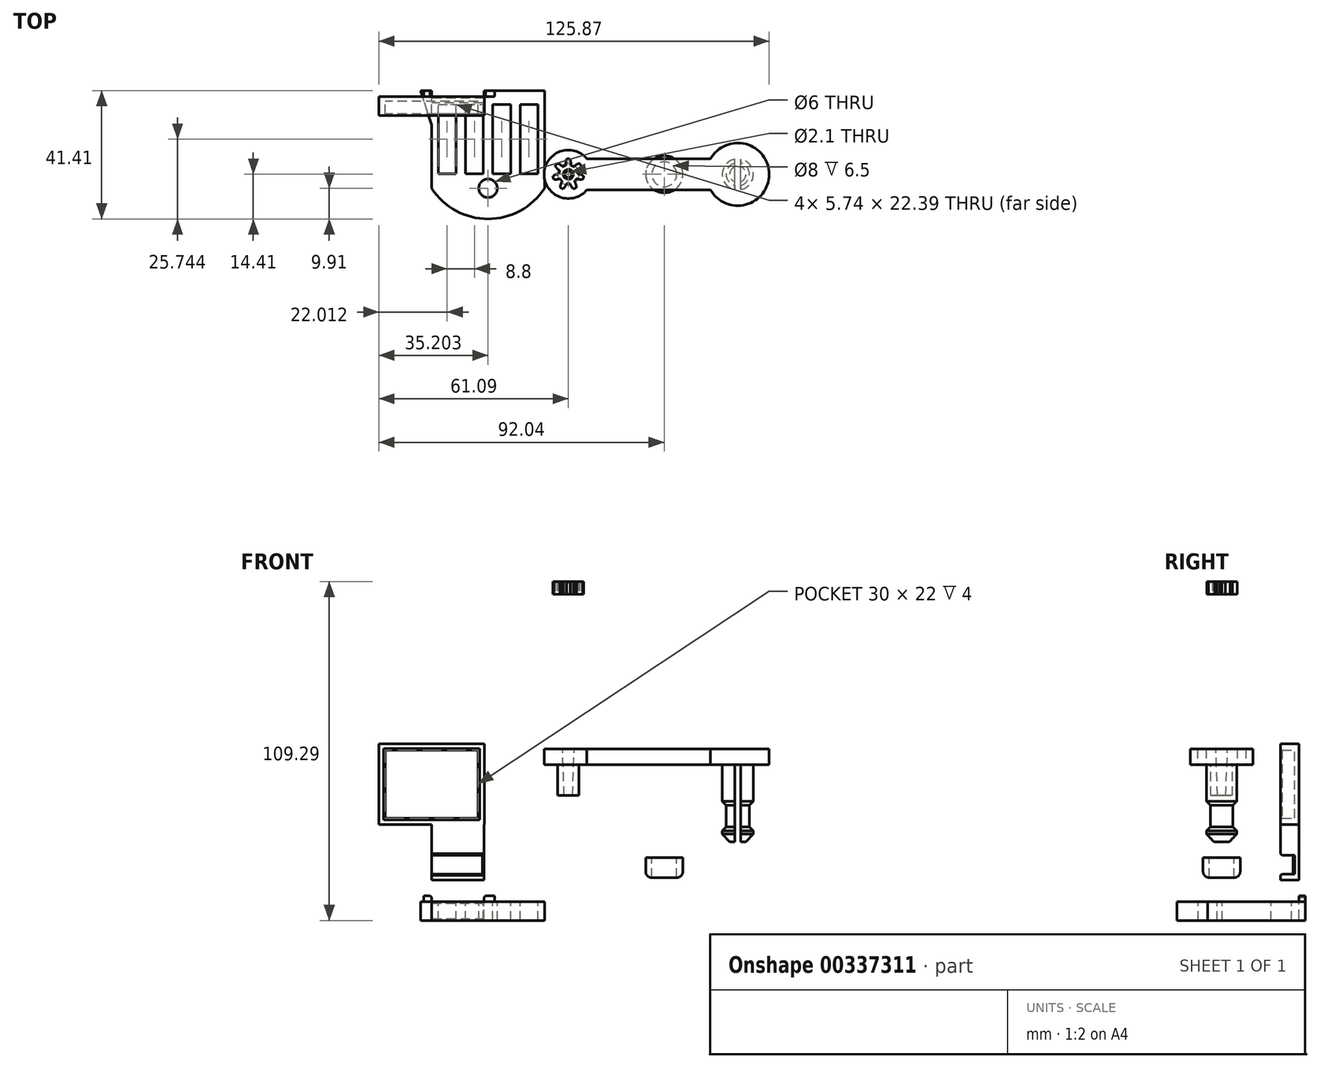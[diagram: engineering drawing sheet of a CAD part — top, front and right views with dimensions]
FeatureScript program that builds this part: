
annotation { "Feature Type Name" : "Feature", "Feature Type Description" : "" }
export const myFeature = defineFeature(function(context is Context, id is Id, definition is map)
    precondition{}
    {
        {
            var Q0;
            Q0=qCreatedBy(makeId("Top.planeOp"),FACE);
            cPlane(context, id + "F0", {"entities" : qUnion([Q0]), "cplaneType" : CPlaneType.OFFSET, "offset" : 25 * mm, "width" : 150 * mm, "height" : 150 * mm});
        }
        {
            var Q0;
            Q0=qCreatedBy(id+"F0.planeOp",FACE);
            var sketch = newSketch(context, id + "F1", { "sketchPlane" : qUnion([Q0])});
            skCircle(sketch, "E0", {"center": v(0, 0) * mm, "radius": 3 * mm, "construction": true});
            skCircle(sketch, "E1", {"center": v(0, 0) * mm, "radius": 5 * mm, "construction": true});
            skArc(sketch, "E2", {"start": v(0.5, 4.97) * mm, "mid": v(0, 5) * mm, "end": v(-0.5, 4.97) * mm});
            skArc(sketch, "E3", {"start": v(-0.5, 4.97) * mm, "mid": v(-0.8, 3.96) * mm, "end": v(-0.77, 2.9) * mm});
            skArc(sketch, "E4.MirrorCS", {"start": v(0.5, 4.97) * mm, "mid": v(0.8, 3.96) * mm, "end": v(0.77, 2.9) * mm});
            skArc(sketch, "E5.1.0", {"start": v(-4.2, 2.71) * mm, "mid": v(-3.6, 1.84) * mm, "end": v(-2.75, 1.2) * mm});
            skArc(sketch, "E5.1.1", {"start": v(-3.58, 3.5) * mm, "mid": v(-3.9, 3.12) * mm, "end": v(-4.2, 2.71) * mm});
            skArc(sketch, "E5.1.2", {"start": v(-3.58, 3.5) * mm, "mid": v(-2.6, 3.1) * mm, "end": v(-1.78, 2.41) * mm});
            skArc(sketch, "E5.2.0", {"start": v(-4.74, -1.6) * mm, "mid": v(-3.68, -1.67) * mm, "end": v(-2.65, -1.4) * mm});
            skArc(sketch, "E5.2.1", {"start": v(-4.96, -0.62) * mm, "mid": v(-4.87, -1.11) * mm, "end": v(-4.74, -1.6) * mm});
            skArc(sketch, "E5.2.2", {"start": v(-4.96, -0.62) * mm, "mid": v(-4.04, -0.1) * mm, "end": v(-3, 0.1) * mm});
            skArc(sketch, "E5.3.0", {"start": v(-1.7, -4.7) * mm, "mid": v(-0.99, -3.92) * mm, "end": v(-0.56, -2.95) * mm});
            skArc(sketch, "E5.3.1", {"start": v(-2.6, -4.27) * mm, "mid": v(-2.17, -4.5) * mm, "end": v(-1.7, -4.7) * mm});
            skArc(sketch, "E5.3.2", {"start": v(-2.6, -4.27) * mm, "mid": v(-2.45, -3.22) * mm, "end": v(-1.95, -2.28) * mm});
            skArc(sketch, "E5.4.0", {"start": v(2.6, -4.27) * mm, "mid": v(2.45, -3.22) * mm, "end": v(1.95, -2.28) * mm});
            skArc(sketch, "E5.4.1", {"start": v(1.7, -4.7) * mm, "mid": v(2.17, -4.5) * mm, "end": v(2.6, -4.27) * mm});
            skArc(sketch, "E5.4.2", {"start": v(1.7, -4.7) * mm, "mid": v(0.99, -3.92) * mm, "end": v(0.56, -2.95) * mm});
            skArc(sketch, "E5.5.0", {"start": v(4.96, -0.62) * mm, "mid": v(4.04, -0.1) * mm, "end": v(3, 0.1) * mm});
            skArc(sketch, "E5.5.1", {"start": v(4.74, -1.6) * mm, "mid": v(4.87, -1.11) * mm, "end": v(4.96, -0.62) * mm});
            skArc(sketch, "E5.5.2", {"start": v(4.74, -1.6) * mm, "mid": v(3.68, -1.67) * mm, "end": v(2.65, -1.4) * mm});
            skArc(sketch, "E5.6.0", {"start": v(3.58, 3.5) * mm, "mid": v(2.6, 3.1) * mm, "end": v(1.78, 2.41) * mm});
            skArc(sketch, "E5.6.1", {"start": v(4.2, 2.71) * mm, "mid": v(3.9, 3.12) * mm, "end": v(3.58, 3.5) * mm});
            skArc(sketch, "E5.6.2", {"start": v(4.2, 2.71) * mm, "mid": v(3.6, 1.84) * mm, "end": v(2.75, 1.2) * mm});
            skArc(sketch, "E6", {"start": v(1.78, 2.41) * mm, "mid": v(1.3, 2.7) * mm, "end": v(0.77, 2.9) * mm});
            skArc(sketch, "E7.1.0", {"start": v(-0.77, 2.9) * mm, "mid": v(-1.3, 2.7) * mm, "end": v(-1.78, 2.41) * mm});
            skArc(sketch, "E7.2.0", {"start": v(-2.75, 1.2) * mm, "mid": v(-2.93, 0.67) * mm, "end": v(-3, 0.1) * mm});
            skArc(sketch, "E7.3.0", {"start": v(-2.65, -1.4) * mm, "mid": v(-2.35, -1.87) * mm, "end": v(-1.95, -2.28) * mm});
            skArc(sketch, "E7.4.0", {"start": v(-0.56, -2.95) * mm, "mid": v(0, -3) * mm, "end": v(0.56, -2.95) * mm});
            skArc(sketch, "E7.5.0", {"start": v(1.95, -2.28) * mm, "mid": v(2.35, -1.87) * mm, "end": v(2.65, -1.4) * mm});
            skArc(sketch, "E7.6.0", {"start": v(3, 0.1) * mm, "mid": v(2.93, 0.67) * mm, "end": v(2.75, 1.2) * mm});
            skSolve(sketch);
        }
        {
            var Q0;
            Q0 = qSketchRegion(id + "F1", true);
            extrude(context, id + "F2", {"entities" : qUnion([Q0]), "depth" : 4 * mm});
        }
        {
            var Q0;
            Q0=qCreatedBy(id+"F0.planeOp",FACE);
            var sketch = newSketch(context, id + "F3", { "sketchPlane" : qUnion([Q0])});
            skCircle(sketch, "E8", {"center": v(0, 0) * mm, "radius": 1.05 * mm});
            skSolve(sketch);
        }
        {
            var Q0;
            Q0 = qSketchRegion(id + "F3", true);
            extrude(context, id + "F4", {"entities" : qUnion([Q0]), "operationType" : NewBodyOperationType.REMOVE, "depth" : 25 * mm});
        }
        {
            var Q0;
            Q0=makeQuery(id+"F4.boolean.opBoolean","COPY",EDGE,{"derivedFrom":makeQuery(id+"F4.opExtrude","CAP_EDGE",EDGE,{"disambiguationData":[OSD([sQuery(id+"F3.wireOp",EDGE,"E8")])],"isStart":true})});
            var Q1;
            Q1=makeQuery(id+"F4.boolean.opBoolean","INTERSECT",EDGE,{"derivedFrom":[makeQuery(id+"F2.opExtrude","CAP_FACE",FACE,{"disambiguationData":[OSD([sQuery(id+"F1.wireOp",EDGE,"E2"),sQuery(id+"F1.wireOp",EDGE,"E3"),sQuery(id+"F1.wireOp",EDGE,"E4.MirrorCS"),sQuery(id+"F1.wireOp",EDGE,"E5.1.0"),sQuery(id+"F1.wireOp",EDGE,"E5.1.1"),sQuery(id+"F1.wireOp",EDGE,"E5.1.2"),sQuery(id+"F1.wireOp",EDGE,"E5.2.0"),sQuery(id+"F1.wireOp",EDGE,"E5.2.1"),sQuery(id+"F1.wireOp",EDGE,"E5.2.2"),sQuery(id+"F1.wireOp",EDGE,"E5.3.0"),sQuery(id+"F1.wireOp",EDGE,"E5.3.1"),sQuery(id+"F1.wireOp",EDGE,"E5.3.2"),sQuery(id+"F1.wireOp",EDGE,"E5.4.0"),sQuery(id+"F1.wireOp",EDGE,"E5.4.1"),sQuery(id+"F1.wireOp",EDGE,"E5.4.2"),sQuery(id+"F1.wireOp",EDGE,"E5.5.0"),sQuery(id+"F1.wireOp",EDGE,"E5.5.1"),sQuery(id+"F1.wireOp",EDGE,"E5.5.2"),sQuery(id+"F1.wireOp",EDGE,"E5.6.0"),sQuery(id+"F1.wireOp",EDGE,"E5.6.1"),sQuery(id+"F1.wireOp",EDGE,"E5.6.2"),sQuery(id+"F1.wireOp",EDGE,"E6"),sQuery(id+"F1.wireOp",EDGE,"E7.1.0"),sQuery(id+"F1.wireOp",EDGE,"E7.2.0"),sQuery(id+"F1.wireOp",EDGE,"E7.3.0"),sQuery(id+"F1.wireOp",EDGE,"E7.4.0"),sQuery(id+"F1.wireOp",EDGE,"E7.5.0"),sQuery(id+"F1.wireOp",EDGE,"E7.6.0")])],"isStart":false}),makeQuery(id+"F4.opExtrude","SWEPT_FACE",FACE,{"disambiguationData":[OSD([sQuery(id+"F3.wireOp",EDGE,"E8")])]})]});
            chamfer(context, id + "F5", {"entities" : qUnion([Q0, Q1]), "width" : .5 * mm, "tangentPropagation" : true});
        }
        {
            var Q0;
            Q0=qCreatedBy(makeId("Top.planeOp"),FACE);
            var sketch = newSketch(context, id + "F6", { "sketchPlane" : qUnion([Q0])});
            skCircle(sketch, "E9", {"center": v(0, 0) * mm, "radius": 15 * mm, "construction": true});
            skCircle(sketch, "E10", {"center": v(0, 0) * mm, "radius": 17 * mm, "construction": true});
            skLineSegment(sketch, "E11", {"start": v(0, 19.59) * mm, "end": v(0, -20.8) * mm, "construction": true});
            skArc(sketch, "E12", {"start": v(0.5, 17) * mm, "mid": v(0, 17) * mm, "end": v(-0.5, 17) * mm});
            skArc(sketch, "E13", {"start": v(-0.5, 17) * mm, "mid": v(-0.8, 16) * mm, "end": v(-0.77, 14.98) * mm});
            skArc(sketch, "E14.MirrorCS", {"start": v(0.5, 17) * mm, "mid": v(0.8, 16) * mm, "end": v(0.77, 14.98) * mm});
            skArc(sketch, "E15.1.0", {"start": v(-4.02, 16.52) * mm, "mid": v(-4.1, 15.5) * mm, "end": v(-3.87, 14.5) * mm});
            skArc(sketch, "E15.1.1", {"start": v(-3.04, 16.73) * mm, "mid": v(-3.53, 16.63) * mm, "end": v(-4.02, 16.52) * mm});
            skArc(sketch, "E15.1.2", {"start": v(-3.04, 16.73) * mm, "mid": v(-2.55, 15.82) * mm, "end": v(-2.36, 14.81) * mm});
            skArc(sketch, "E15.2.0", {"start": v(-7.37, 15.32) * mm, "mid": v(-7.24, 14.3) * mm, "end": v(-6.8, 13.37) * mm});
            skArc(sketch, "E15.2.1", {"start": v(-6.45, 15.73) * mm, "mid": v(-6.91, 15.53) * mm, "end": v(-7.37, 15.32) * mm});
            skArc(sketch, "E15.2.2", {"start": v(-6.45, 15.73) * mm, "mid": v(-5.78, 14.95) * mm, "end": v(-5.39, 14) * mm});
            skArc(sketch, "E15.3.0", {"start": v(-10.4, 13.45) * mm, "mid": v(-10.05, 12.48) * mm, "end": v(-9.43, 11.67) * mm});
            skArc(sketch, "E15.3.1", {"start": v(-9.58, 14.04) * mm, "mid": v(-10, 13.75) * mm, "end": v(-10.4, 13.45) * mm});
            skArc(sketch, "E15.3.2", {"start": v(-9.58, 14.04) * mm, "mid": v(-8.77, 13.42) * mm, "end": v(-8.18, 12.57) * mm});
            skArc(sketch, "E15.4.0", {"start": v(-12.96, 11) * mm, "mid": v(-12.43, 10.12) * mm, "end": v(-11.65, 9.45) * mm});
            skArc(sketch, "E15.4.1", {"start": v(-12.3, 11.74) * mm, "mid": v(-12.63, 11.38) * mm, "end": v(-12.96, 11) * mm});
            skArc(sketch, "E15.4.2", {"start": v(-12.3, 11.74) * mm, "mid": v(-11.36, 11.3) * mm, "end": v(-10.62, 10.6) * mm});
            skArc(sketch, "E15.5.0", {"start": v(-14.97, 8.06) * mm, "mid": v(-14.26, 7.31) * mm, "end": v(-13.36, 6.82) * mm});
            skArc(sketch, "E15.5.1", {"start": v(-14.47, 8.93) * mm, "mid": v(-14.72, 8.5) * mm, "end": v(-14.97, 8.06) * mm});
            skArc(sketch, "E15.5.2", {"start": v(-14.47, 8.93) * mm, "mid": v(-13.47, 8.7) * mm, "end": v(-12.59, 8.16) * mm});
            skArc(sketch, "E15.6.0", {"start": v(-16.32, 4.78) * mm, "mid": v(-15.47, 4.19) * mm, "end": v(-14.48, 3.9) * mm});
            skArc(sketch, "E15.6.1", {"start": v(-16, 5.73) * mm, "mid": v(-16.17, 5.25) * mm, "end": v(-16.32, 4.78) * mm});
            skArc(sketch, "E15.6.2", {"start": v(-16, 5.73) * mm, "mid": v(-14.98, 5.7) * mm, "end": v(-14, 5.36) * mm});
            skArc(sketch, "E15.7.0", {"start": v(-16.95, 1.28) * mm, "mid": v(-16, 0.88) * mm, "end": v(-14.98, 0.8) * mm});
            skArc(sketch, "E15.7.1", {"start": v(-16.85, 2.27) * mm, "mid": v(-16.9, 1.78) * mm, "end": v(-16.95, 1.28) * mm});
            skArc(sketch, "E15.7.2", {"start": v(-16.85, 2.27) * mm, "mid": v(-15.84, 2.47) * mm, "end": v(-14.82, 2.33) * mm});
            skArc(sketch, "E15.8.0", {"start": v(-16.85, -2.27) * mm, "mid": v(-15.84, -2.47) * mm, "end": v(-14.82, -2.33) * mm});
            skArc(sketch, "E15.8.1", {"start": v(-16.95, -1.28) * mm, "mid": v(-16.9, -1.78) * mm, "end": v(-16.85, -2.27) * mm});
            skArc(sketch, "E15.8.2", {"start": v(-16.95, -1.28) * mm, "mid": v(-16, -0.88) * mm, "end": v(-14.98, -0.8) * mm});
            skArc(sketch, "E15.9.0", {"start": v(-16, -5.73) * mm, "mid": v(-14.98, -5.7) * mm, "end": v(-14, -5.36) * mm});
            skArc(sketch, "E15.9.1", {"start": v(-16.32, -4.78) * mm, "mid": v(-16.17, -5.25) * mm, "end": v(-16, -5.73) * mm});
            skArc(sketch, "E15.9.2", {"start": v(-16.32, -4.78) * mm, "mid": v(-15.47, -4.19) * mm, "end": v(-14.48, -3.9) * mm});
            skArc(sketch, "E15.10.0", {"start": v(-14.47, -8.93) * mm, "mid": v(-13.47, -8.7) * mm, "end": v(-12.59, -8.16) * mm});
            skArc(sketch, "E15.10.1", {"start": v(-14.97, -8.06) * mm, "mid": v(-14.72, -8.5) * mm, "end": v(-14.47, -8.93) * mm});
            skArc(sketch, "E15.10.2", {"start": v(-14.97, -8.06) * mm, "mid": v(-14.26, -7.31) * mm, "end": v(-13.36, -6.82) * mm});
            skArc(sketch, "E15.11.0", {"start": v(-12.3, -11.74) * mm, "mid": v(-11.36, -11.3) * mm, "end": v(-10.62, -10.6) * mm});
            skArc(sketch, "E15.11.1", {"start": v(-12.96, -11) * mm, "mid": v(-12.63, -11.38) * mm, "end": v(-12.3, -11.74) * mm});
            skArc(sketch, "E15.11.2", {"start": v(-12.96, -11) * mm, "mid": v(-12.43, -10.12) * mm, "end": v(-11.65, -9.45) * mm});
            skArc(sketch, "E15.12.0", {"start": v(-9.58, -14.04) * mm, "mid": v(-8.77, -13.42) * mm, "end": v(-8.18, -12.57) * mm});
            skArc(sketch, "E15.12.1", {"start": v(-10.4, -13.45) * mm, "mid": v(-10, -13.75) * mm, "end": v(-9.58, -14.04) * mm});
            skArc(sketch, "E15.12.2", {"start": v(-10.4, -13.45) * mm, "mid": v(-10.05, -12.48) * mm, "end": v(-9.43, -11.67) * mm});
            skArc(sketch, "E15.13.0", {"start": v(-6.45, -15.73) * mm, "mid": v(-5.78, -14.95) * mm, "end": v(-5.39, -14) * mm});
            skArc(sketch, "E15.13.1", {"start": v(-7.37, -15.32) * mm, "mid": v(-6.91, -15.53) * mm, "end": v(-6.45, -15.73) * mm});
            skArc(sketch, "E15.13.2", {"start": v(-7.37, -15.32) * mm, "mid": v(-7.24, -14.3) * mm, "end": v(-6.8, -13.37) * mm});
            skArc(sketch, "E15.14.0", {"start": v(-3.04, -16.73) * mm, "mid": v(-2.55, -15.82) * mm, "end": v(-2.36, -14.81) * mm});
            skArc(sketch, "E15.14.1", {"start": v(-4.02, -16.52) * mm, "mid": v(-3.53, -16.63) * mm, "end": v(-3.04, -16.73) * mm});
            skArc(sketch, "E15.14.2", {"start": v(-4.02, -16.52) * mm, "mid": v(-4.1, -15.5) * mm, "end": v(-3.87, -14.5) * mm});
            skArc(sketch, "E15.15.0", {"start": v(0.5, -17) * mm, "mid": v(0.8, -16) * mm, "end": v(0.77, -14.98) * mm});
            skArc(sketch, "E15.15.1", {"start": v(-0.5, -17) * mm, "mid": v(0, -17) * mm, "end": v(0.5, -17) * mm});
            skArc(sketch, "E15.15.2", {"start": v(-0.5, -17) * mm, "mid": v(-0.8, -16) * mm, "end": v(-0.77, -14.98) * mm});
            skArc(sketch, "E15.16.0", {"start": v(4.02, -16.52) * mm, "mid": v(4.1, -15.5) * mm, "end": v(3.87, -14.5) * mm});
            skArc(sketch, "E15.16.1", {"start": v(3.04, -16.73) * mm, "mid": v(3.53, -16.63) * mm, "end": v(4.02, -16.52) * mm});
            skArc(sketch, "E15.16.2", {"start": v(3.04, -16.73) * mm, "mid": v(2.55, -15.82) * mm, "end": v(2.36, -14.81) * mm});
            skArc(sketch, "E15.17.0", {"start": v(7.37, -15.32) * mm, "mid": v(7.24, -14.3) * mm, "end": v(6.8, -13.37) * mm});
            skArc(sketch, "E15.17.1", {"start": v(6.45, -15.73) * mm, "mid": v(6.91, -15.53) * mm, "end": v(7.37, -15.32) * mm});
            skArc(sketch, "E15.17.2", {"start": v(6.45, -15.73) * mm, "mid": v(5.78, -14.95) * mm, "end": v(5.39, -14) * mm});
            skArc(sketch, "E15.18.0", {"start": v(10.4, -13.45) * mm, "mid": v(10.05, -12.48) * mm, "end": v(9.43, -11.67) * mm});
            skArc(sketch, "E15.18.1", {"start": v(9.58, -14.04) * mm, "mid": v(10, -13.75) * mm, "end": v(10.4, -13.45) * mm});
            skArc(sketch, "E15.18.2", {"start": v(9.58, -14.04) * mm, "mid": v(8.77, -13.42) * mm, "end": v(8.18, -12.57) * mm});
            skArc(sketch, "E15.19.0", {"start": v(12.96, -11) * mm, "mid": v(12.43, -10.12) * mm, "end": v(11.65, -9.45) * mm});
            skArc(sketch, "E15.19.1", {"start": v(12.3, -11.74) * mm, "mid": v(12.63, -11.38) * mm, "end": v(12.96, -11) * mm});
            skArc(sketch, "E15.19.2", {"start": v(12.3, -11.74) * mm, "mid": v(11.36, -11.3) * mm, "end": v(10.62, -10.6) * mm});
            skArc(sketch, "E15.20.0", {"start": v(14.97, -8.06) * mm, "mid": v(14.26, -7.31) * mm, "end": v(13.36, -6.82) * mm});
            skArc(sketch, "E15.20.1", {"start": v(14.47, -8.93) * mm, "mid": v(14.72, -8.5) * mm, "end": v(14.97, -8.06) * mm});
            skArc(sketch, "E15.20.2", {"start": v(14.47, -8.93) * mm, "mid": v(13.47, -8.7) * mm, "end": v(12.59, -8.16) * mm});
            skArc(sketch, "E15.21.0", {"start": v(16.32, -4.78) * mm, "mid": v(15.47, -4.19) * mm, "end": v(14.48, -3.9) * mm});
            skArc(sketch, "E15.21.1", {"start": v(16, -5.73) * mm, "mid": v(16.17, -5.25) * mm, "end": v(16.32, -4.78) * mm});
            skArc(sketch, "E15.21.2", {"start": v(16, -5.73) * mm, "mid": v(14.98, -5.7) * mm, "end": v(14, -5.36) * mm});
            skArc(sketch, "E15.22.0", {"start": v(16.95, -1.28) * mm, "mid": v(16, -0.88) * mm, "end": v(14.98, -0.8) * mm});
            skArc(sketch, "E15.22.1", {"start": v(16.85, -2.27) * mm, "mid": v(16.9, -1.78) * mm, "end": v(16.95, -1.28) * mm});
            skArc(sketch, "E15.22.2", {"start": v(16.85, -2.27) * mm, "mid": v(15.84, -2.47) * mm, "end": v(14.82, -2.33) * mm});
            skArc(sketch, "E15.23.0", {"start": v(16.85, 2.27) * mm, "mid": v(15.84, 2.47) * mm, "end": v(14.82, 2.33) * mm});
            skArc(sketch, "E15.23.1", {"start": v(16.95, 1.28) * mm, "mid": v(16.9, 1.78) * mm, "end": v(16.85, 2.27) * mm});
            skArc(sketch, "E15.23.2", {"start": v(16.95, 1.28) * mm, "mid": v(16, 0.88) * mm, "end": v(14.98, 0.8) * mm});
            skArc(sketch, "E15.24.0", {"start": v(16, 5.73) * mm, "mid": v(14.98, 5.7) * mm, "end": v(14, 5.36) * mm});
            skArc(sketch, "E15.24.1", {"start": v(16.32, 4.78) * mm, "mid": v(16.17, 5.25) * mm, "end": v(16, 5.73) * mm});
            skArc(sketch, "E15.24.2", {"start": v(16.32, 4.78) * mm, "mid": v(15.47, 4.19) * mm, "end": v(14.48, 3.9) * mm});
            skArc(sketch, "E15.25.0", {"start": v(14.47, 8.93) * mm, "mid": v(13.47, 8.7) * mm, "end": v(12.59, 8.16) * mm});
            skArc(sketch, "E15.25.1", {"start": v(14.97, 8.06) * mm, "mid": v(14.72, 8.5) * mm, "end": v(14.47, 8.93) * mm});
            skArc(sketch, "E15.25.2", {"start": v(14.97, 8.06) * mm, "mid": v(14.26, 7.31) * mm, "end": v(13.36, 6.82) * mm});
            skArc(sketch, "E15.26.0", {"start": v(12.3, 11.74) * mm, "mid": v(11.36, 11.3) * mm, "end": v(10.62, 10.6) * mm});
            skArc(sketch, "E15.26.1", {"start": v(12.96, 11) * mm, "mid": v(12.63, 11.38) * mm, "end": v(12.3, 11.74) * mm});
            skArc(sketch, "E15.26.2", {"start": v(12.96, 11) * mm, "mid": v(12.43, 10.12) * mm, "end": v(11.65, 9.45) * mm});
            skArc(sketch, "E15.27.0", {"start": v(9.58, 14.04) * mm, "mid": v(8.77, 13.42) * mm, "end": v(8.18, 12.57) * mm});
            skArc(sketch, "E15.27.1", {"start": v(10.4, 13.45) * mm, "mid": v(10, 13.75) * mm, "end": v(9.58, 14.04) * mm});
            skArc(sketch, "E15.27.2", {"start": v(10.4, 13.45) * mm, "mid": v(10.05, 12.48) * mm, "end": v(9.43, 11.67) * mm});
            skArc(sketch, "E15.28.0", {"start": v(6.45, 15.73) * mm, "mid": v(5.78, 14.95) * mm, "end": v(5.39, 14) * mm});
            skArc(sketch, "E15.28.1", {"start": v(7.37, 15.32) * mm, "mid": v(6.91, 15.53) * mm, "end": v(6.45, 15.73) * mm});
            skArc(sketch, "E15.28.2", {"start": v(7.37, 15.32) * mm, "mid": v(7.24, 14.3) * mm, "end": v(6.8, 13.37) * mm});
            skArc(sketch, "E15.29.0", {"start": v(3.04, 16.73) * mm, "mid": v(2.55, 15.82) * mm, "end": v(2.36, 14.81) * mm});
            skArc(sketch, "E15.29.1", {"start": v(4.02, 16.52) * mm, "mid": v(3.53, 16.63) * mm, "end": v(3.04, 16.73) * mm});
            skArc(sketch, "E15.29.2", {"start": v(4.02, 16.52) * mm, "mid": v(4.1, 15.5) * mm, "end": v(3.87, 14.5) * mm});
            skArc(sketch, "E16", {"start": v(2.36, 14.81) * mm, "mid": v(1.57, 14.93) * mm, "end": v(0.77, 14.98) * mm});
            skArc(sketch, "E17.1.0", {"start": v(-0.77, 14.98) * mm, "mid": v(-1.57, 14.93) * mm, "end": v(-2.36, 14.81) * mm});
            skArc(sketch, "E17.2.0", {"start": v(-3.87, 14.5) * mm, "mid": v(-4.64, 14.28) * mm, "end": v(-5.39, 14) * mm});
            skArc(sketch, "E17.3.0", {"start": v(-6.8, 13.37) * mm, "mid": v(-7.5, 13) * mm, "end": v(-8.18, 12.57) * mm});
            skArc(sketch, "E17.4.0", {"start": v(-9.43, 11.67) * mm, "mid": v(-10.05, 11.16) * mm, "end": v(-10.62, 10.6) * mm});
            skArc(sketch, "E17.5.0", {"start": v(-11.65, 9.45) * mm, "mid": v(-12.15, 8.83) * mm, "end": v(-12.59, 8.16) * mm});
            skArc(sketch, "E17.6.0", {"start": v(-13.36, 6.82) * mm, "mid": v(-13.72, 6.1) * mm, "end": v(-14, 5.36) * mm});
            skArc(sketch, "E17.7.0", {"start": v(-14.48, 3.9) * mm, "mid": v(-14.69, 3.12) * mm, "end": v(-14.82, 2.33) * mm});
            skArc(sketch, "E17.8.0", {"start": v(-14.98, 0.8) * mm, "mid": v(-15.02, 0) * mm, "end": v(-14.98, -0.8) * mm});
            skArc(sketch, "E17.9.0", {"start": v(-14.82, -2.33) * mm, "mid": v(-14.69, -3.12) * mm, "end": v(-14.48, -3.9) * mm});
            skArc(sketch, "E17.10.0", {"start": v(-14, -5.36) * mm, "mid": v(-13.72, -6.1) * mm, "end": v(-13.36, -6.82) * mm});
            skArc(sketch, "E17.11.0", {"start": v(-12.59, -8.16) * mm, "mid": v(-12.15, -8.83) * mm, "end": v(-11.65, -9.45) * mm});
            skArc(sketch, "E17.12.0", {"start": v(-10.62, -10.6) * mm, "mid": v(-10.05, -11.16) * mm, "end": v(-9.43, -11.67) * mm});
            skArc(sketch, "E17.13.0", {"start": v(-8.18, -12.57) * mm, "mid": v(-7.5, -13) * mm, "end": v(-6.8, -13.37) * mm});
            skArc(sketch, "E17.14.0", {"start": v(-5.39, -14) * mm, "mid": v(-4.64, -14.28) * mm, "end": v(-3.87, -14.5) * mm});
            skArc(sketch, "E17.15.0", {"start": v(-2.36, -14.81) * mm, "mid": v(-1.57, -14.93) * mm, "end": v(-0.77, -14.98) * mm});
            skArc(sketch, "E17.16.0", {"start": v(0.77, -14.98) * mm, "mid": v(1.57, -14.93) * mm, "end": v(2.36, -14.81) * mm});
            skArc(sketch, "E17.17.0", {"start": v(3.87, -14.5) * mm, "mid": v(4.64, -14.28) * mm, "end": v(5.39, -14) * mm});
            skArc(sketch, "E17.18.0", {"start": v(6.8, -13.37) * mm, "mid": v(7.5, -13) * mm, "end": v(8.18, -12.57) * mm});
            skArc(sketch, "E17.19.0", {"start": v(9.43, -11.67) * mm, "mid": v(10.05, -11.16) * mm, "end": v(10.62, -10.6) * mm});
            skArc(sketch, "E17.20.0", {"start": v(11.65, -9.45) * mm, "mid": v(12.15, -8.83) * mm, "end": v(12.59, -8.16) * mm});
            skArc(sketch, "E17.21.0", {"start": v(13.36, -6.82) * mm, "mid": v(13.72, -6.1) * mm, "end": v(14, -5.36) * mm});
            skArc(sketch, "E17.22.0", {"start": v(14.48, -3.9) * mm, "mid": v(14.69, -3.12) * mm, "end": v(14.82, -2.33) * mm});
            skArc(sketch, "E17.23.0", {"start": v(14.98, -0.8) * mm, "mid": v(15.02, 0) * mm, "end": v(14.98, 0.8) * mm});
            skArc(sketch, "E17.24.0", {"start": v(14.82, 2.33) * mm, "mid": v(14.69, 3.12) * mm, "end": v(14.48, 3.9) * mm});
            skArc(sketch, "E17.25.0", {"start": v(14, 5.36) * mm, "mid": v(13.72, 6.1) * mm, "end": v(13.36, 6.82) * mm});
            skArc(sketch, "E17.26.0", {"start": v(12.59, 8.16) * mm, "mid": v(12.15, 8.83) * mm, "end": v(11.65, 9.45) * mm});
            skArc(sketch, "E17.27.0", {"start": v(10.62, 10.6) * mm, "mid": v(10.05, 11.16) * mm, "end": v(9.43, 11.67) * mm});
            skArc(sketch, "E17.28.0", {"start": v(8.18, 12.57) * mm, "mid": v(7.5, 13) * mm, "end": v(6.8, 13.37) * mm});
            skArc(sketch, "E17.29.0", {"start": v(5.39, 14) * mm, "mid": v(4.64, 14.28) * mm, "end": v(3.87, 14.5) * mm});
            skSolve(sketch);
        }
        {
            var Q0;
            Q0 = qSketchRegion(id + "F6", true);
            extrude(context, id + "F7", {"entities" : qUnion([Q0]), "depth" : 4 * mm});
        }
        {
            var Q0;
            Q0=qCreatedBy(makeId("Top.planeOp"),FACE);
            var sketch = newSketch(context, id + "F8", { "sketchPlane" : qUnion([Q0])});
            skCircle(sketch, "E18", {"center": v(0, 0) * mm, "radius": 1.5 * mm});
            skSolve(sketch);
        }
        {
            var Q0;
            Q0 = qSketchRegion(id + "F8", true);
            extrude(context, id + "F9", {"entities" : qUnion([Q0]), "operationType" : NewBodyOperationType.ADD, "oppositeDirection" : true, "depth" : 25 * mm});
        }
        {
            var Q0;
            Q0=makeQuery(id+"F9.opExtrude","CAP_EDGE",EDGE,{"disambiguationData":[OSD([sQuery(id+"F8.wireOp",EDGE,"E18")])],"isStart":true});
            var Q1;
            Q1=makeQuery(id+"F9.opExtrude","CAP_EDGE",EDGE,{"disambiguationData":[OSD([sQuery(id+"F8.wireOp",EDGE,"E18")])],"isStart":false});
            chamfer(context, id + "F10", {"entities" : qUnion([Q0, Q1]), "width" : 0.8 * mm, "tangentPropagation" : true});
        }
        {
            var Q0;
            Q0=qCreatedBy(makeId("Front.planeOp"),FACE);
            cPlane(context, id + "F11", {"entities" : qUnion([Q0]), "cplaneType" : CPlaneType.OFFSET, "offset" : 25 * mm, "oppositeDirection" : true, "width" : 150 * mm, "height" : 150 * mm});
        }
        {
            var Q0;
            Q0=qCreatedBy(id+"F11.planeOp",FACE);
            var sketch = newSketch(context, id + "F12", { "sketchPlane" : qUnion([Q0])});
            skLineSegment(sketch, "E19.bottom", {"start": v(-59.09, -25.3) * mm, "end": v(-29.09, -25.3) * mm});
            skLineSegment(sketch, "E19.top", {"start": v(-59.09, -47.3) * mm, "end": v(-29.09, -47.3) * mm});
            skLineSegment(sketch, "E19.left", {"start": v(-59.09, -25.3) * mm, "end": v(-59.09, -47.3) * mm});
            skLineSegment(sketch, "E19.right", {"start": v(-29.09, -25.3) * mm, "end": v(-29.09, -47.3) * mm});
            skLineSegment(sketch, "E20.bottom", {"start": v(-61.09, -23.3) * mm, "end": v(-27.09, -23.3) * mm});
            skLineSegment(sketch, "E20.top", {"start": v(-61.09, -49.3) * mm, "end": v(-27.09, -49.3) * mm});
            skLineSegment(sketch, "E20.left", {"start": v(-61.09, -23.3) * mm, "end": v(-61.09, -49.3) * mm});
            skLineSegment(sketch, "E20.right", {"start": v(-27.09, -23.3) * mm, "end": v(-27.09, -49.3) * mm});
            skLineSegment(sketch, "E21", {"start": v(-68.97, -36.3) * mm, "end": v(0, -36.3) * mm, "construction": true});
            skLineSegment(sketch, "E22", {"start": v(-44.09, -5.6) * mm, "end": v(-44.09, -66.71) * mm, "construction": true});
            skLineSegment(sketch, "E23.bottom", {"start": v(-44.09, -49.3) * mm, "end": v(-27.14, -49.3) * mm});
            skLineSegment(sketch, "E23.top", {"start": v(-44.09, -67.3) * mm, "end": v(-27.14, -67.3) * mm});
            skLineSegment(sketch, "E23.left", {"start": v(-44.09, -49.3) * mm, "end": v(-44.09, -67.3) * mm});
            skLineSegment(sketch, "E23.right", {"start": v(-27.14, -49.3) * mm, "end": v(-27.14, -67.3) * mm});
            skSolve(sketch);
        }
        {
            var Q0;
            Q0=makeQuery(id+"F12.imprint","IMPRINT",FACE,{"disambiguationData":[TD([[makeQuery(id+"F12.imprint","IMPRINT",EDGE,{"derivedFrom":sQuery(id+"F12.wireOp",EDGE,"E19.bottom")}),-1.0]])]});
            var Q1;
            Q1=makeQuery(id+"F12.imprint","IMPRINT",FACE,{"disambiguationData":[TD([[makeQuery(id+"F12.imprint","IMPRINT",EDGE,{"derivedFrom":sQuery(id+"F12.wireOp",EDGE,"E19.bottom")}),1.0]])]});
            extrude(context, id + "F13", {"entities" : qUnion([Q0, Q1]), "depth" : 1.5 * mm});
        }
        {
            var Q0;
            Q0 = qSketchRegion(id + "F12", true);
            extrude(context, id + "F14", {"entities" : qUnion([Q0]), "operationType" : NewBodyOperationType.ADD, "depth" : 6 * mm});
        }
        {
            var Q0;
            {var subQ0=sQuery(id+"F12.wireOp",EDGE,"E20.top");var subQ1=sQuery(id+"F12.wireOp",EDGE,"E23.bottom");Q0=makeQuery(id+"F14.boolean.opBoolean","MERGE",FACE,{"derivedFrom":[makeQuery(id+"F13.opExtrude","SWEPT_FACE",FACE,{"disambiguationData":[OSD([subQ0,subQ1])]}),makeQuery(id+"F14.opExtrude","SWEPT_FACE",FACE,{"disambiguationData":[OSD([subQ0]),TDD([makeQuery(id+"F12.imprint","IMPRINT",EDGE,{"disambiguationData":[TD([[makeQuery(id+"F12.imprint","INTERSECT",VERTEX,{"derivedFrom":[subQ0,sQuery(id+"F12.wireOp",EDGE,"E20.left")]}),-1.0]])],"derivedFrom":subQ0})])]})]});}
            cPlane(context, id + "F15", {"entities" : qUnion([Q0]), "cplaneType" : CPlaneType.OFFSET, "offset" : 25 * mm, "width" : 150 * mm, "height" : 150 * mm});
        }
        {
            var Q0;
            Q0=qCreatedBy(id+"F15.planeOp",FACE);
            var sketch = newSketch(context, id + "F16", { "sketchPlane" : qUnion([Q0])});
            skLineSegment(sketch, "E24.bottom", {"start": v(-44.09, -25) * mm, "end": v(-7.69, -25) * mm});
            skLineSegment(sketch, "E24.left", {"start": v(-44.09, -25) * mm, "end": v(-44.09, 4.5) * mm});
            skLineSegment(sketch, "E24.right", {"start": v(-7.69, -25) * mm, "end": v(-7.69, 4.5) * mm});
            skArc(sketch, "E25", {"start": v(-7.69, 4.5) * mm, "mid": v(-25.89, 14.41) * mm, "end": v(-44.09, 4.5) * mm});
            skLineSegment(sketch, "E26", {"start": v(-25.89, 22.07) * mm, "end": v(-25.89, -31.93) * mm, "construction": true});
            skLineSegment(sketch, "E27", {"start": v(-44.09, 4.5) * mm, "end": v(-7.69, 4.5) * mm, "construction": true});
            skCircle(sketch, "E28", {"center": v(-25.89, 4.5) * mm, "radius": 3 * mm});
            skLineSegment(sketch, "E29", {"start": v(-44.09, -15.93) * mm, "end": v(-47.61, -27) * mm});
            skLineSegment(sketch, "E30", {"start": v(-47.61, -27) * mm, "end": v(-44.13, -27) * mm});
            skLineSegment(sketch, "E31", {"start": v(-44.13, -27) * mm, "end": v(-44.09, -25) * mm});
            skLineSegment(sketch, "E32", {"start": v(-27.14, -25) * mm, "end": v(-27.14, -27) * mm});
            skLineSegment(sketch, "E33", {"start": v(-27.14, -27) * mm, "end": v(-7.69, -27) * mm});
            skLineSegment(sketch, "E34", {"start": v(-7.69, -27) * mm, "end": v(-7.69, -25) * mm});
            skLineSegment(sketch, "E35.bottom", {"start": v(-41.95, -0.14) * mm, "end": v(-36.2, -0.14) * mm});
            skLineSegment(sketch, "E35.top", {"start": v(-41.95, -22.53) * mm, "end": v(-36.2, -22.53) * mm});
            skLineSegment(sketch, "E35.left", {"start": v(-41.95, -0.14) * mm, "end": v(-41.95, -22.53) * mm});
            skLineSegment(sketch, "E35.right", {"start": v(-36.2, -0.14) * mm, "end": v(-36.2, -22.53) * mm});
            skLineSegment(sketch, "E36.1.0.0", {"start": v(-27.4, -0.14) * mm, "end": v(-27.4, -22.53) * mm});
            skLineSegment(sketch, "E36.1.0.1", {"start": v(-33.15, -0.14) * mm, "end": v(-27.4, -0.14) * mm});
            skLineSegment(sketch, "E36.1.0.2", {"start": v(-33.15, -0.14) * mm, "end": v(-33.15, -22.53) * mm});
            skLineSegment(sketch, "E36.1.0.3", {"start": v(-33.15, -22.53) * mm, "end": v(-27.4, -22.53) * mm});
            skLineSegment(sketch, "E36.2.0.0", {"start": v(-18.6, -0.14) * mm, "end": v(-18.6, -22.53) * mm});
            skLineSegment(sketch, "E36.2.0.1", {"start": v(-24.35, -0.14) * mm, "end": v(-18.6, -0.14) * mm});
            skLineSegment(sketch, "E36.2.0.2", {"start": v(-24.35, -0.14) * mm, "end": v(-24.35, -22.53) * mm});
            skLineSegment(sketch, "E36.2.0.3", {"start": v(-24.35, -22.53) * mm, "end": v(-18.6, -22.53) * mm});
            skLineSegment(sketch, "E36.3.0.0", {"start": v(-9.8, -0.14) * mm, "end": v(-9.8, -22.53) * mm});
            skLineSegment(sketch, "E36.3.0.1", {"start": v(-15.55, -0.14) * mm, "end": v(-9.8, -0.14) * mm});
            skLineSegment(sketch, "E36.3.0.2", {"start": v(-15.55, -0.14) * mm, "end": v(-15.55, -22.53) * mm});
            skLineSegment(sketch, "E36.3.0.3", {"start": v(-15.55, -22.53) * mm, "end": v(-9.8, -22.53) * mm});
            skLineSegment(sketch, "E36.direction1", {"start": v(-36.2, -22.53) * mm, "end": v(-27.4, -22.53) * mm, "construction": true});
            skSolve(sketch);
        }
        {
            var Q0;
            Q0=makeQuery(id+"F16.imprint","IMPRINT",FACE,{"disambiguationData":[TD([[makeQuery(id+"F16.imprint","IMPRINT",EDGE,{"derivedFrom":sQuery(id+"F16.wireOp",EDGE,"E24.bottom")}),1.0]])]});
            var Q1;
            {var subQ2=sQuery(id+"F16.wireOp",EDGE,"E29");Q1=makeQuery(id+"F16.imprint","IMPRINT",FACE,{"disambiguationData":[TD([[makeQuery(id+"F16.imprint","IMPRINT",EDGE,{"derivedFrom":subQ2}),1.0]])]});}
            var Q2;
            {var subQ2=sQuery(id+"F16.wireOp",EDGE,"E32");Q2=makeQuery(id+"F16.imprint","IMPRINT",FACE,{"disambiguationData":[TD([[makeQuery(id+"F16.imprint","IMPRINT",EDGE,{"derivedFrom":subQ2}),1.0]])]});}
            extrude(context, id + "F17", {"entities" : qUnion([Q0, Q1, Q2]), "depth" : 6 * mm});
        }
        {
            var Q0;
            Q0=makeQuery(id+"F14.opExtrude","SWEPT_FACE",FACE,{"disambiguationData":[OSD([sQuery(id+"F12.wireOp",EDGE,"E23.left")])]});
            cPlane(context, id + "F18", {"entities" : qUnion([Q0]), "cplaneType" : CPlaneType.OFFSET, "offset" : 0 * mm, "width" : 150 * mm, "height" : 150 * mm});
        }
        {
            var Q0;
            Q0=qCreatedBy(id+"F18.planeOp",FACE);
            var sketch = newSketch(context, id + "F19", { "sketchPlane" : qUnion([Q0])});
            skLineSegment(sketch, "E37.bottom", {"start": v(-17.2, -59.3) * mm, "end": v(-23, -59.3) * mm});
            skLineSegment(sketch, "E37.top", {"start": v(-17.2, -65.3) * mm, "end": v(-23, -65.3) * mm});
            skLineSegment(sketch, "E37.left", {"start": v(-17.2, -59.3) * mm, "end": v(-17.2, -65.3) * mm});
            skLineSegment(sketch, "E37.right", {"start": v(-23, -59.3) * mm, "end": v(-23, -65.3) * mm});
            skSolve(sketch);
        }
        {
            var Q0;
            Q0 = qSketchRegion(id + "F19", true);
            extrude(context, id + "F20", {"entities" : qUnion([Q0]), "operationType" : NewBodyOperationType.REMOVE, "oppositeDirection" : true, "depth" : 25 * mm});
        }
        {
            var Q0;
            Q0=qCreatedBy(id+"F15.planeOp",FACE);
            var sketch = newSketch(context, id + "F21", { "sketchPlane" : qUnion([Q0])});
            skLineSegment(sketch, "E38.bottom", {"start": v(-46.65, -25) * mm, "end": v(-44.09, -25) * mm});
            skLineSegment(sketch, "E38.top", {"start": v(-46.65, -27) * mm, "end": v(-44.13, -27) * mm});
            skLineSegment(sketch, "E38.left", {"start": v(-46.65, -25) * mm, "end": v(-46.65, -27) * mm});
            skLineSegment(sketch, "E38.right", {"start": v(-44.09, -25) * mm, "end": v(-44.13, -27) * mm});
            skLineSegment(sketch, "E39.bottom", {"start": v(-27.14, -25) * mm, "end": v(-23.77, -25) * mm});
            skLineSegment(sketch, "E39.top", {"start": v(-27.14, -27) * mm, "end": v(-23.77, -27) * mm});
            skLineSegment(sketch, "E39.left", {"start": v(-27.14, -25) * mm, "end": v(-27.14, -27) * mm});
            skLineSegment(sketch, "E39.right", {"start": v(-23.77, -25) * mm, "end": v(-23.77, -27) * mm});
            skSolve(sketch);
        }
        {
            var Q0;
            Q0 = qSketchRegion(id + "F21", true);
            extrude(context, id + "F22", {"entities" : qUnion([Q0]), "operationType" : NewBodyOperationType.ADD, "oppositeDirection" : true, "depth" : 2 * mm});
        }
        {
            var Q0;
            Q0=makeQuery(id+"F22.opExtrude","CAP_EDGE",EDGE,{"disambiguationData":[OSD([sQuery(id+"F21.wireOp",EDGE,"E39.left")])],"isStart":false});
            var Q1;
            Q1=makeQuery(id+"F22.opExtrude","CAP_EDGE",EDGE,{"disambiguationData":[OSD([sQuery(id+"F21.wireOp",EDGE,"E38.right")])],"isStart":false});
            var Q2;
            Q2=makeQuery(id+"F20.boolean.opBoolean","INTERSECT",EDGE,{"derivedFrom":[makeQuery(id+"F14.opExtrude","CAP_FACE",FACE,{"disambiguationData":[OSD([sQuery(id+"F12.wireOp",EDGE,"E19.bottom"),sQuery(id+"F12.wireOp",EDGE,"E19.top"),sQuery(id+"F12.wireOp",EDGE,"E19.left"),sQuery(id+"F12.wireOp",EDGE,"E19.right"),sQuery(id+"F12.wireOp",EDGE,"E20.bottom"),sQuery(id+"F12.wireOp",EDGE,"E20.top"),sQuery(id+"F12.wireOp",EDGE,"E20.left"),sQuery(id+"F12.wireOp",EDGE,"E20.right"),sQuery(id+"F12.wireOp",EDGE,"E23.top"),sQuery(id+"F12.wireOp",EDGE,"E23.left"),sQuery(id+"F12.wireOp",EDGE,"E23.right")])],"isStart":false}),makeQuery(id+"F20.opExtrude","SWEPT_FACE",FACE,{"disambiguationData":[OSD([sQuery(id+"F19.wireOp",EDGE,"E37.top")])]})]});
            var Q3;
            Q3=makeQuery(id+"F20.boolean.opBoolean","INTERSECT",EDGE,{"derivedFrom":[makeQuery(id+"F14.opExtrude","CAP_FACE",FACE,{"disambiguationData":[OSD([sQuery(id+"F12.wireOp",EDGE,"E19.bottom"),sQuery(id+"F12.wireOp",EDGE,"E19.top"),sQuery(id+"F12.wireOp",EDGE,"E19.left"),sQuery(id+"F12.wireOp",EDGE,"E19.right"),sQuery(id+"F12.wireOp",EDGE,"E20.bottom"),sQuery(id+"F12.wireOp",EDGE,"E20.top"),sQuery(id+"F12.wireOp",EDGE,"E20.left"),sQuery(id+"F12.wireOp",EDGE,"E20.right"),sQuery(id+"F12.wireOp",EDGE,"E23.top"),sQuery(id+"F12.wireOp",EDGE,"E23.left"),sQuery(id+"F12.wireOp",EDGE,"E23.right")])],"isStart":false}),makeQuery(id+"F20.opExtrude","SWEPT_FACE",FACE,{"disambiguationData":[OSD([sQuery(id+"F19.wireOp",EDGE,"E37.bottom")])]})]});
            var Q4;
            Q4=makeQuery(id+"F17.opExtrude","CAP_EDGE",EDGE,{"disambiguationData":[OSD([sQuery(id+"F16.wireOp",EDGE,"E24.bottom")])],"isStart":true});
            var Q5;
            Q5=makeQuery(id+"F17.opExtrude","CAP_EDGE",EDGE,{"disambiguationData":[OSD([sQuery(id+"F16.wireOp",EDGE,"E24.bottom")])],"isStart":false});
            var Q6;
            Q6=makeQuery(id+"F20.boolean.opBoolean","COPY",EDGE,{"derivedFrom":makeQuery(id+"F20.opExtrude","CAP_EDGE",EDGE,{"disambiguationData":[OSD([sQuery(id+"F19.wireOp",EDGE,"E37.right")])],"isStart":true})});
            var Q7;
            Q7=makeQuery(id+"F20.boolean.opBoolean","INTERSECT",EDGE,{"derivedFrom":[makeQuery(id+"F14.opExtrude","SWEPT_FACE",FACE,{"disambiguationData":[OSD([sQuery(id+"F12.wireOp",EDGE,"E23.right")])]}),makeQuery(id+"F20.opExtrude","SWEPT_FACE",FACE,{"disambiguationData":[OSD([sQuery(id+"F19.wireOp",EDGE,"E37.right")])]})]});
            var Q8;
            Q8=makeQuery(id+"F14.opExtrude","CAP_EDGE",EDGE,{"disambiguationData":[OSD([sQuery(id+"F12.wireOp",EDGE,"E19.right")])],"isStart":false});
            var Q9;
            Q9=makeQuery(id+"F14.opExtrude","CAP_EDGE",EDGE,{"disambiguationData":[OSD([sQuery(id+"F12.wireOp",EDGE,"E19.bottom")])],"isStart":false});
            var Q10;
            Q10=makeQuery(id+"F14.opExtrude","CAP_EDGE",EDGE,{"disambiguationData":[OSD([sQuery(id+"F12.wireOp",EDGE,"E19.top")])],"isStart":false});
            var Q11;
            Q11=makeQuery(id+"F14.opExtrude","CAP_EDGE",EDGE,{"disambiguationData":[OSD([sQuery(id+"F12.wireOp",EDGE,"E19.left")])],"isStart":false});
            chamfer(context, id + "F23", {"entities" : qUnion([Q0, Q1, Q2, Q3, Q4, Q5, Q6, Q7, Q8, Q9, Q10, Q11]), "width" : 0.5 * mm, "tangentPropagation" : true});
        }
        {
            var Q0;
            Q0=qCreatedBy(makeId("Top.planeOp"),FACE);
            cPlane(context, id + "F24", {"entities" : qUnion([Q0]), "cplaneType" : CPlaneType.OFFSET, "offset" : 30 * mm, "oppositeDirection" : true, "width" : 150 * mm, "height" : 150 * mm});
        }
        {
            var Q0;
            Q0=qCreatedBy(id+"F24.planeOp",FACE);
            var sketch = newSketch(context, id + "F25", { "sketchPlane" : qUnion([Q0])});
            skCircle(sketch, "E40", {"center": v(0, 0) * mm, "radius": 7.82 * mm});
            skCircle(sketch, "E41", {"center": v(54.67, 0) * mm, "radius": 10.11 * mm});
            skLineSegment(sketch, "E42", {"start": v(6, -5) * mm, "end": v(45.88, -5) * mm});
            skLineSegment(sketch, "E43", {"start": v(6, 5) * mm, "end": v(45.88, 5) * mm});
            skLineSegment(sketch, "E44", {"start": v(54.67, -13.85) * mm, "end": v(54.67, 16.05) * mm, "construction": true});
            skSolve(sketch);
        }
        {
            var Q0;
            Q0 = qSketchRegion(id + "F25", true);
            extrude(context, id + "F26", {"entities" : qUnion([Q0]), "operationType" : NewBodyOperationType.ADD, "depth" : 5 * mm});
        }
        {
            var Q0;
            Q0=makeQuery(id+"F26.opExtrude","CAP_FACE",FACE,{"disambiguationData":[OSD([sQuery(id+"F25.wireOp",EDGE,"E40"),sQuery(id+"F25.wireOp",EDGE,"E41"),sQuery(id+"F25.wireOp",EDGE,"E42"),sQuery(id+"F25.wireOp",EDGE,"E43")])],"isStart":true});
            var sketch = newSketch(context, id + "F27", { "sketchPlane" : qUnion([Q0])});
            skCircle(sketch, "E45", {"center": v(0, 0) * mm, "radius": 3.44 * mm});
            skSolve(sketch);
        }
        {
            var Q0;
            Q0 = qSketchRegion(id + "F27", true);
            extrude(context, id + "F28", {"entities" : qUnion([Q0]), "operationType" : NewBodyOperationType.ADD, "depth" : 10 * mm});
        }
        {
            var Q0;
            Q0=makeQuery(id+"F28.opExtrude","CAP_FACE",FACE,{"disambiguationData":[OSD([sQuery(id+"F27.wireOp",EDGE,"E45")])],"isStart":false});
            var sketch = newSketch(context, id + "F29", { "sketchPlane" : qUnion([Q0])});
            skCircle(sketch, "E46", {"center": v(0, 0) * mm, "radius": 1.35 * mm});
            skSolve(sketch);
        }
        {
            var Q0;
            Q0 = qSketchRegion(id + "F29", true);
            extrude(context, id + "F30", {"entities" : qUnion([Q0]), "operationType" : NewBodyOperationType.REMOVE, "oppositeDirection" : true, "depth" : 15 * mm, "hasDraft" : true, "draftAngle" : 2 * degree});
        }
        {
            var Q0;
            Q0=makeQuery(id+"F26.opExtrude","CAP_FACE",FACE,{"disambiguationData":[OSD([sQuery(id+"F25.wireOp",EDGE,"E40"),sQuery(id+"F25.wireOp",EDGE,"E41"),sQuery(id+"F25.wireOp",EDGE,"E42"),sQuery(id+"F25.wireOp",EDGE,"E43")])],"isStart":true});
            var sketch = newSketch(context, id + "F31", { "sketchPlane" : qUnion([Q0])});
            skCircle(sketch, "E47", {"center": v(54.67, 0) * mm, "radius": 5 * mm});
            skSolve(sketch);
        }
        {
            var Q0;
            Q0 = qSketchRegion(id + "F31", true);
            extrude(context, id + "F32", {"entities" : qUnion([Q0]), "operationType" : NewBodyOperationType.ADD, "depth" : 25 * mm});
        }
        {
            var Q0;
            Q0=makeQuery(id+"F32.opExtrude","CAP_FACE",FACE,{"disambiguationData":[OSD([sQuery(id+"F31.wireOp",EDGE,"E47")])],"isStart":false});
            var sketch = newSketch(context, id + "F33", { "sketchPlane" : qUnion([Q0])});
            skLineSegment(sketch, "E48.bottom", {"start": v(53.65, 5.4) * mm, "end": v(55.65, 5.4) * mm});
            skLineSegment(sketch, "E48.top", {"start": v(53.65, -5.66) * mm, "end": v(55.65, -5.66) * mm});
            skLineSegment(sketch, "E48.left", {"start": v(53.65, 5.4) * mm, "end": v(53.65, -5.66) * mm});
            skLineSegment(sketch, "E48.right", {"start": v(55.65, 5.4) * mm, "end": v(55.65, -5.66) * mm});
            skSolve(sketch);
        }
        {
            var Q0;
            Q0 = qSketchRegion(id + "F33", true);
            extrude(context, id + "F34", {"entities" : qUnion([Q0]), "operationType" : NewBodyOperationType.REMOVE, "oppositeDirection" : true, "depth" : 25 * mm});
        }
        {
            var Q0;
            Q0=qCreatedBy(makeId("Front.planeOp"),FACE);
            var sketch = newSketch(context, id + "F35", { "sketchPlane" : qUnion([Q0])});
            skLineSegment(sketch, "E49", {"start": v(56.43, -55.94) * mm, "end": v(59.96, -52.04) * mm});
            skLineSegment(sketch, "E50", {"start": v(59.96, -52.04) * mm, "end": v(59.96, -55.94) * mm});
            skLineSegment(sketch, "E51", {"start": v(59.96, -55.94) * mm, "end": v(56.43, -55.94) * mm});
            skLineSegment(sketch, "E52", {"start": v(60.04, -41.5) * mm, "end": v(58.42, -43.13) * mm});
            skLineSegment(sketch, "E53", {"start": v(60.04, -51.75) * mm, "end": v(60.04, -41.5) * mm});
            skLineSegment(sketch, "E54", {"start": v(58.42, -43.13) * mm, "end": v(58.42, -50.13) * mm});
            skLineSegment(sketch, "E55", {"start": v(58.42, -50.13) * mm, "end": v(60.04, -51.75) * mm});
            skSolve(sketch);
        }
        {
            var Q0;
            Q0=makeQuery(id+"F35.imprint","IMPRINT",FACE,{"disambiguationData":[TD([[makeQuery(id+"F35.imprint","IMPRINT",EDGE,{"derivedFrom":sQuery(id+"F35.wireOp",EDGE,"E52")}),1.0]])]});
            var Q1;
            Q1=makeQuery(id+"F35.imprint","IMPRINT",FACE,{"disambiguationData":[TD([[makeQuery(id+"F35.imprint","IMPRINT",EDGE,{"derivedFrom":sQuery(id+"F35.wireOp",EDGE,"E49")}),-1.0]])]});
            var Q2;
            {var subQ0=sQuery(id+"F33.wireOp",EDGE,"E48.right");var subQ1=sQuery(id+"F31.wireOp",EDGE,"E47");Q2=makeQuery(id+"F34.boolean.opBoolean","SPLIT",FACE,{"disambiguationData":[TD([makeQuery(id+"F34.opExtrude","SWEPT_FACE",FACE,{"disambiguationData":[OSD([subQ0])]})])],"derivedFrom":makeQuery(id+"F32.opExtrude","SWEPT_FACE",FACE,{"disambiguationData":[OSD([subQ1])]})});}
            revolve(context, id + "F36", {"operationType" : NewBodyOperationType.REMOVE, "entities" : qUnion([Q0, Q1]), "axis" : qUnion([Q2]), "revolveType" : RevolveType.FULL, "oppositeDirection" : true});
        }
        {
            var Q0;
            {var subQ0=sQuery(id+"F31.wireOp",EDGE,"E47");Q0=makeQuery(id+"F34.boolean.opBoolean","SPLIT",FACE,{"disambiguationData":[TD([makeQuery(id+"F34.opExtrude","SWEPT_FACE",FACE,{"disambiguationData":[OSD([sQuery(id+"F33.wireOp",EDGE,"E48.left")])]})])],"derivedFrom":makeQuery(id+"F32.opExtrude","CAP_FACE",FACE,{"disambiguationData":[OSD([subQ0])],"isStart":false})});}
            cPlane(context, id + "F37", {"entities" : qUnion([Q0]), "cplaneType" : CPlaneType.OFFSET, "offset" : 5 * mm, "width" : 150 * mm, "height" : 150 * mm});
        }
        {
            var Q0;
            Q0=qCreatedBy(id+"F37.planeOp",FACE);
            var sketch = newSketch(context, id + "F38", { "sketchPlane" : qUnion([Q0])});
            skCircle(sketch, "E56", {"center": v(30.95, 0) * mm, "radius": 4 * mm});
            skCircle(sketch, "E57", {"center": v(30.95, 0) * mm, "radius": 6 * mm});
            skSolve(sketch);
        }
        {
            var Q0;
            Q0 = qSketchRegion(id + "F38", true);
            extrude(context, id + "F39", {"entities" : qUnion([Q0]), "depth" : 6.5 * mm});
        }
        {
            var Q0;
            Q0=makeQuery(id+"F39.opExtrude","CAP_EDGE",EDGE,{"disambiguationData":[OSD([sQuery(id+"F38.wireOp",EDGE,"E57")])],"isStart":false});
            fillet(context, id + "F40", {"entities" : qUnion([Q0]), "radius" : 2 * mm, "tangentPropagation" : true, "allowEdgeOverflow" : false});
        }
        {
            var Q0;
            Q0=qCreatedBy(makeId("Right.planeOp"),FACE);
            var sketch = newSketch(context, id + "F41", { "sketchPlane" : qUnion([Q0])});
            skLineSegment(sketch, "E58", {"start": v(-13.96, 4.43) * mm, "end": v(-17.3, 2.9) * mm});
            skLineSegment(sketch, "E59", {"start": v(-17.3, 2.9) * mm, "end": v(-17.3, 4.52) * mm});
            skLineSegment(sketch, "E60", {"start": v(-17.3, 4.52) * mm, "end": v(-13.96, 4.43) * mm});
            skSolve(sketch);
        }
        {
            var Q0;
            Q0=makeQuery(id+"F41.imprint","IMPRINT",FACE,{"disambiguationData":[TD([[makeQuery(id+"F41.imprint","IMPRINT",EDGE,{"derivedFrom":sQuery(id+"F41.wireOp",EDGE,"E58")}),-1.0]])]});
            var Q1;
            Q1=makeQuery(id+"F9.opExtrude","SWEPT_FACE",FACE,{"disambiguationData":[OSD([sQuery(id+"F8.wireOp",EDGE,"E18")])]});
            revolve(context, id + "F42", {"operationType" : NewBodyOperationType.REMOVE, "entities" : qUnion([Q0]), "axis" : qUnion([Q1]), "revolveType" : RevolveType.FULL, "oppositeDirection" : true});
        }
    });
